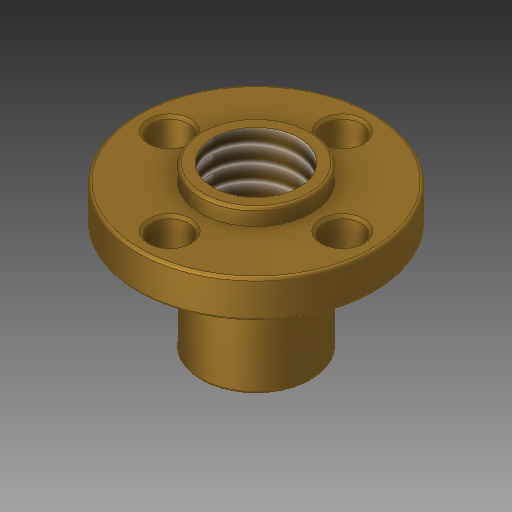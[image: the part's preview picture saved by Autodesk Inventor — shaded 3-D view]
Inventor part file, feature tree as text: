
AUTODESK INVENTOR PART (.ipt)
format: ipt  version: 2019 (Build 230136000, 136)  size: 209,408 bytes
history: native  units: mm
features: sketch x2, revolve x1, extrude x1, chamfer x1, fillet x1, thread x1
ambient origin geometry x8: Origin, YZ Plane, XZ Plane, XY Plane, X Axis, Y Axis, Z Axis, Center Point
bodies: Solid1 (feature_tree)
feature tree (7):
  revolve  "Revolution1"  [1 undecoded]
  extrude  "Extrusion1"  Depth=11.0mm
  chamfer  "Chamfer1"  Distance=4.0mm
  fillet  "Fillet1"  Radius=5.15mm
  thread  "Thread1"  [1 undecoded]
  sketch  "Sketch1"  dims[d1=3.5mm d2=1.5mm]
  sketch  "Sketch2"  dims[d3=15.0mm d4=11.0mm d5=4.0mm d6=5.15mm d7=90.0deg d8=16.0mm d9=3.5mm d10=10.0mm d11=0.0mm d12=0.25mm d13=2.0mm d14=45.0deg d15=0.25mm d16=10.0mm d17=0.0mm]
note: 2 required parameter values undecoded (feature->parameter linkage not recoverable at this tier; creation-order binding heuristic only, values carry confidence <= 0.55)